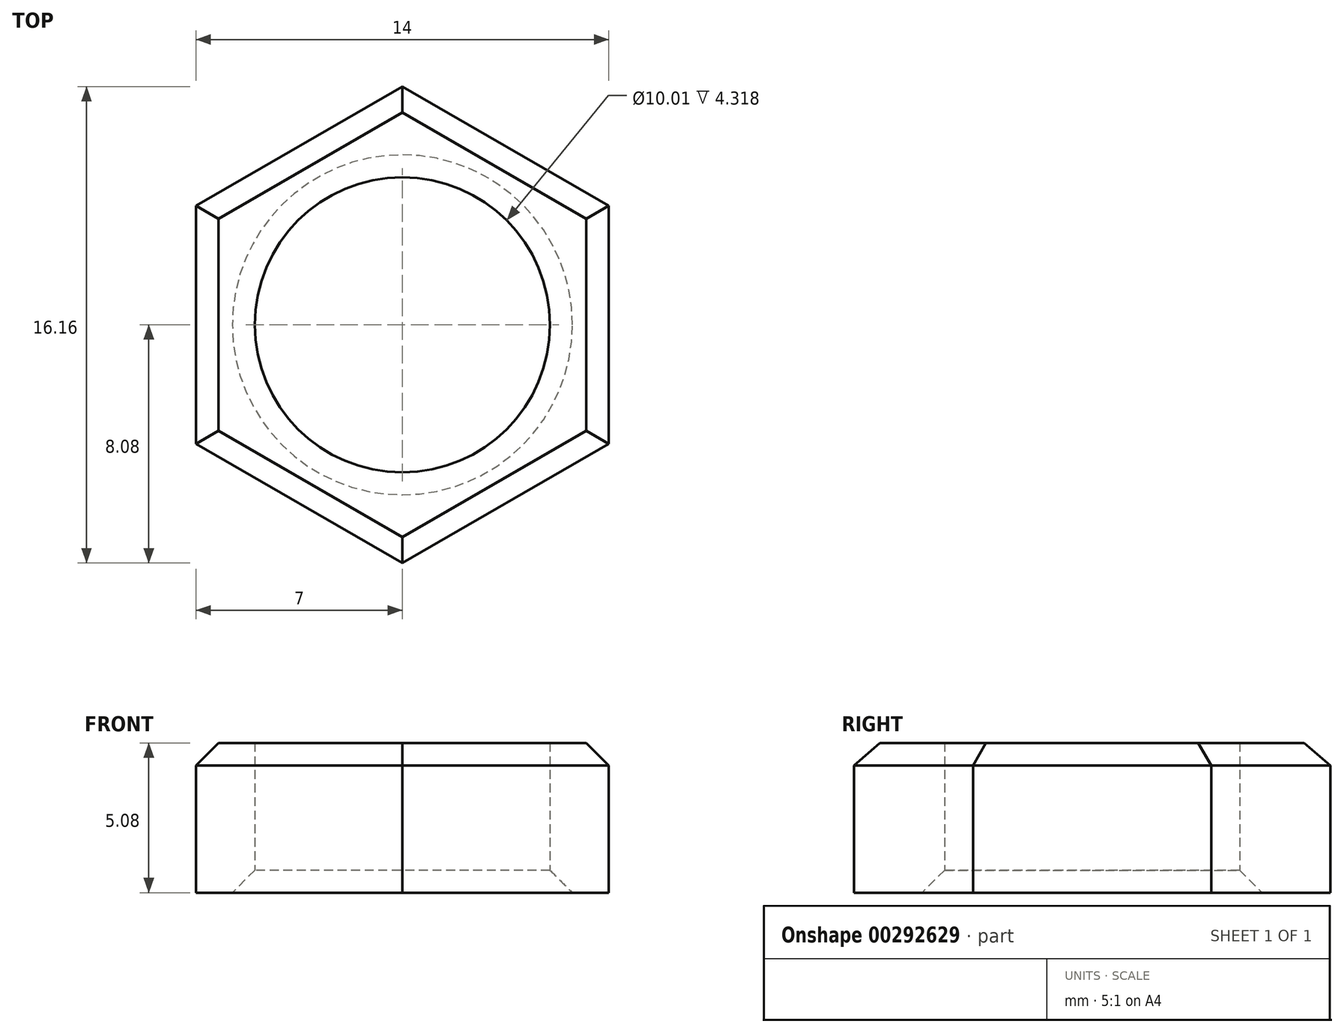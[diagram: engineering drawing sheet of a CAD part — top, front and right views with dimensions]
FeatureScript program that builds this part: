
annotation { "Feature Type Name" : "Feature", "Feature Type Description" : "" }
export const myFeature = defineFeature(function(context is Context, id is Id, definition is map)
    precondition{}
    {
        {
            var Q0;
            Q0=qCreatedBy(makeId("Top.planeOp"),FACE);
            var sketch = newSketch(context, id + "F0", { "sketchPlane" : qUnion([Q0])});
            skCircle(sketch, "E0.cCircle", {"center": v(0, 0) * mm, "radius": 8.08 * mm, "construction": true});
            skLineSegment(sketch, "E0.0", {"start": v(-7, 4.04) * mm, "end": v(0, 8.08) * mm});
            skLineSegment(sketch, "E0.1", {"start": v(0, 8.08) * mm, "end": v(7, 4.04) * mm});
            skLineSegment(sketch, "E0.2", {"start": v(7, 4.04) * mm, "end": v(7, -4.04) * mm});
            skLineSegment(sketch, "E0.3", {"start": v(7, -4.04) * mm, "end": v(0, -8.08) * mm});
            skLineSegment(sketch, "E0.4", {"start": v(0, -8.08) * mm, "end": v(-7, -4.04) * mm});
            skLineSegment(sketch, "E0.5", {"start": v(-7, -4.04) * mm, "end": v(-7, 4.04) * mm});
            skCircle(sketch, "E1", {"center": v(0, 0) * mm, "radius": 5 * mm});
            skSolve(sketch);
        }
        {
            var Q0;
            Q0=makeQuery(id+"F0.imprint","IMPRINT",FACE,{"disambiguationData":[TD([[makeQuery(id+"F0.imprint","IMPRINT",EDGE,{"derivedFrom":sQuery(id+"F0.wireOp",EDGE,"E0.0")}),-1.0]])]});
            extrude(context, id + "F1", {"entities" : qUnion([Q0]), "depth" : 5.08 * mm});
        }
        {
            var Q0;
            Q0=makeQuery(id+"F1.opExtrude","CAP_EDGE",EDGE,{"disambiguationData":[OSD([sQuery(id+"F0.wireOp",EDGE,"E0.0")])],"isStart":false});
            var Q1;
            Q1=makeQuery(id+"F1.opExtrude","CAP_EDGE",EDGE,{"disambiguationData":[OSD([sQuery(id+"F0.wireOp",EDGE,"E0.5")])],"isStart":false});
            var Q2;
            Q2=makeQuery(id+"F1.opExtrude","CAP_EDGE",EDGE,{"disambiguationData":[OSD([sQuery(id+"F0.wireOp",EDGE,"E0.4")])],"isStart":false});
            var Q3;
            Q3=makeQuery(id+"F1.opExtrude","CAP_EDGE",EDGE,{"disambiguationData":[OSD([sQuery(id+"F0.wireOp",EDGE,"E0.3")])],"isStart":false});
            var Q4;
            Q4=makeQuery(id+"F1.opExtrude","CAP_EDGE",EDGE,{"disambiguationData":[OSD([sQuery(id+"F0.wireOp",EDGE,"E0.2")])],"isStart":false});
            var Q5;
            Q5=makeQuery(id+"F1.opExtrude","CAP_EDGE",EDGE,{"disambiguationData":[OSD([sQuery(id+"F0.wireOp",EDGE,"E0.1")])],"isStart":false});
            chamfer(context, id + "F2", {"entities" : qUnion([Q0, Q1, Q2, Q3, Q4, Q5]), "width" : 0.76 * mm, "tangentPropagation" : true});
        }
        {
            var Q0;
            Q0=makeQuery(id+"F1.opExtrude","CAP_EDGE",EDGE,{"disambiguationData":[OSD([sQuery(id+"F0.wireOp",EDGE,"E1")])],"isStart":true});
            chamfer(context, id + "F3", {"entities" : qUnion([Q0]), "width" : 0.76 * mm, "tangentPropagation" : true});
        }
    });
